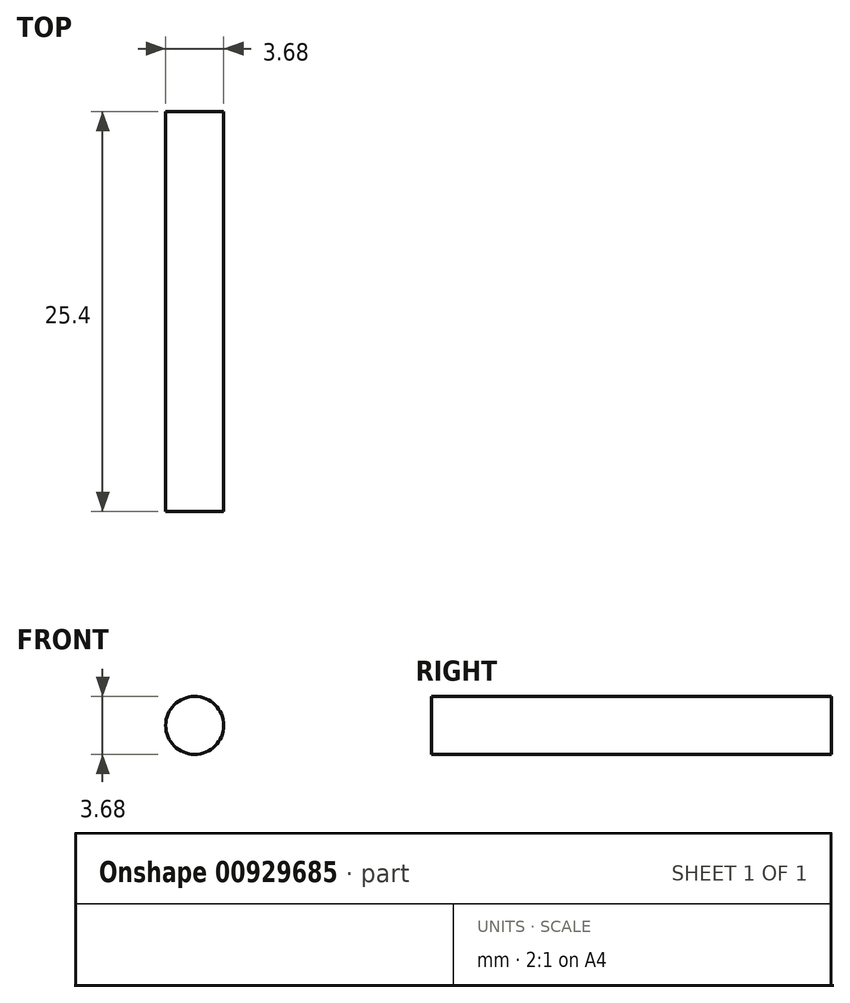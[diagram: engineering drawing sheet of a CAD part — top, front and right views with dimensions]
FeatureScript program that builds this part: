
annotation { "Feature Type Name" : "Feature", "Feature Type Description" : "" }
export const myFeature = defineFeature(function(context is Context, id is Id, definition is map)
    precondition{}
    {
        {
            var Q0;
            Q0=qCreatedBy(makeId("Front.planeOp"),FACE);
            var sketch = newSketch(context, id + "F0", { "sketchPlane" : qUnion([Q0])});
            skCircle(sketch, "E0", {"center": v(0, 0) * mm, "radius": 1.84 * mm});
            skSolve(sketch);
        }
        {
            var Q0;
            Q0=qSketchRegion(id+"F0",true);
            extrude(context, id + "F1", {"entities" : qUnion([Q0]), "depth" : 25.4 * mm, "offsetDistance" : 25.4 * mm});
        }
    });
